# Revit family: CEC3(4RED+1-2RJ45)
name_source: partatom
category: Aparatos eléctricos
revit_build: Autodesk Revit 2016 (Build: 20150220_1215(x64)
units: mm (PartAtom-declared; Revit-internal decimal feet)

## family parameters
Anfitrión = Cara
Compartido = No
Corte con vacíos al cargar = No
Cota de conector redondo = Diámetro de uso
Mantener orientación de anotación = No
Número OmniClass = 23.80.50.11.11
Punto de cálculo de habitación = No
Tipo de pieza = Normal
Título OmniClass = Receptacle Terminal Units

## types (3) — shared parameters
CEC2 + CEM2 (AltoxLargoxAncho) = 128 x 150 x 63,50 (94 con tapa)
CEC3 + CEM3 (AltoxLargoxAncho) = 128 x 208 x 63,50 (94 con tapa)
CEC4 + CEM4 (AltoxLargoxAncho) = 128 x 267 x 63,50 (94 con tapa)
CEC5 + CEM5 (AltoxLargoxAncho) = 128 x 325 x 63,50 (94 con tapa)
Capacidad = 2-5 módulos Plus
Carga eléctrica = Potencia
Compatibilidad = Gama Plus
Composición = Cubeta, Marco, Tornillería tapa (4ud), Anclajes x2, Embellecedores x2, Separador
Código de montaje = D5020100
Descripción = Caja de conexiones empotrable CE Plus
Elevación por defecto = 1200 mm
Fabricante = MMCONECTA
Factor de potencia = 1
Instalación = Empotrado
Modelo = CEC3(4RED+1-2RJ45)
Normativas = UNE 60670-1:2006 + CORR. 2008 / Marcado CE
Polos = 1
Potencia aparente = 3500 W
URL = http://www.mmconecta.com
Voltaje = 230 V
Ø tubos G = 25 mm  [stored 0.082021 ft]
Ø tubos P = 20 mm  [stored 0.0656168 ft]

## per-type parameters (varying)
| type | Acabado | Materia prima |
| Módulo /4 - Blanco | Blanco nieve RAL9019 | Policarbonato libre de halógenos |
| Módulo /6 - Grafito | Grafito RAL7021 | Policarbonato libre de halógenos |
| Módulo /9 - Aluminio | Aluminio anodizado | Aluminio anodizado |

note: [stored X ft] marks values corroborated as IEEE doubles in the binary element streams (Revit-internal decimal feet)

## geometry (parser evidence)
native form markers: Blend x3
no freeform markers — native parametric forms only
